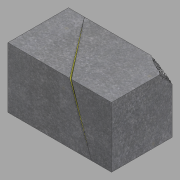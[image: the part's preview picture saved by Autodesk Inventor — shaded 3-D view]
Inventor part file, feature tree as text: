
AUTODESK INVENTOR PART (.ipt)
format: ipt  version: 2022.1 (Build 261234020, 234B)  size: 663,040 bytes
history: native  units: in
note: dims shown in document units (in); Inventor stores cm internally (conversion verified against a paired STEP export)
features: other x3, sketch x3, extrude x1, loft x1
ambient origin geometry x8: Origin, YZ Plane, XZ Plane, XY Plane, X Axis, Y Axis, Z Axis, Center Point
bodies: Solid1 (feature_tree)
feature tree (8):
  other  "2nd.ipt"
  extrude  "Extrusion1"  Depth=1.0in TaperAngle=0.0deg
  loft  "Loft1"
  other  "Solid1::2nd.ipt"
  other  "TaggingFeature1"
  sketch  "Sketch1"  dims[d0=0.3937in d1=1.0in d2=0.0in]
  sketch  "Sketch2"  dims[d3=0.0in d4=90.0deg d5=0.0in d6=90.0deg]
  sketch  "Sketch3"
